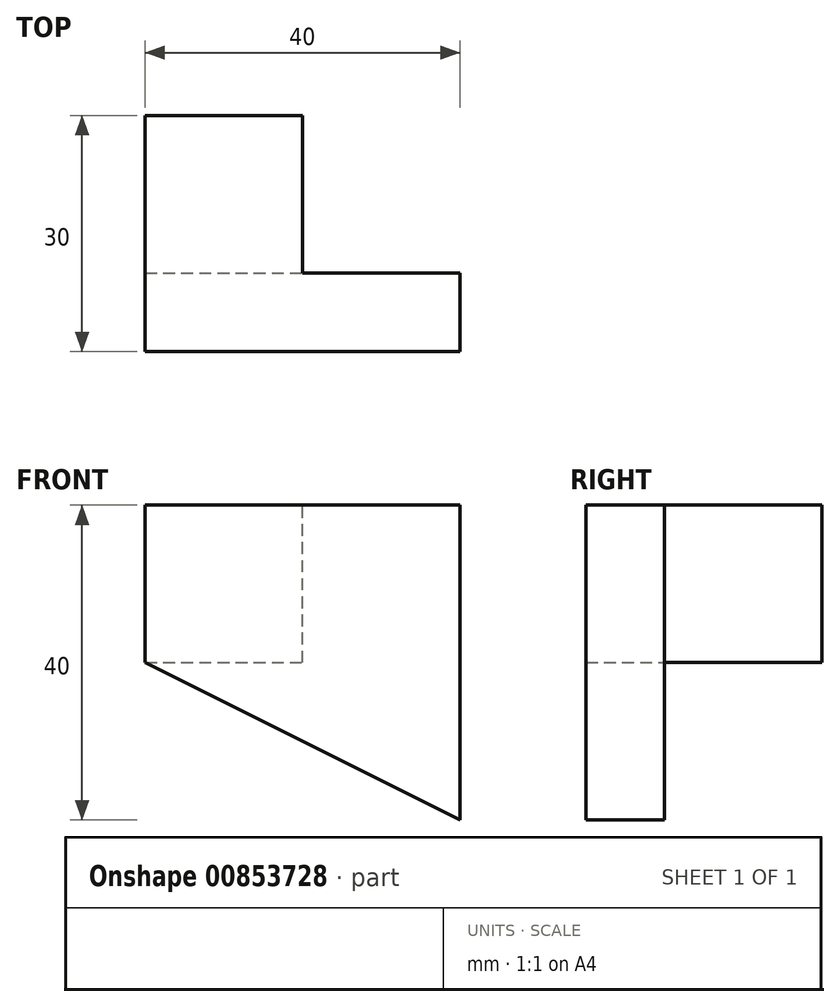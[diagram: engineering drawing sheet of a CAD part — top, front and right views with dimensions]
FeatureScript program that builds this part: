
annotation { "Feature Type Name" : "Feature", "Feature Type Description" : "" }
export const myFeature = defineFeature(function(context is Context, id is Id, definition is map)
    precondition{}
    {
        {
            var Q0;
            Q0=qCreatedBy(makeId("Front.planeOp"),FACE);
            var sketch = newSketch(context, id + "F0", { "sketchPlane" : qUnion([Q0])});
            skLineSegment(sketch, "E0.bottom", {"start": v(0, 0) * mm, "end": v(20, 0) * mm});
            skLineSegment(sketch, "E0.top", {"start": v(0, 20) * mm, "end": v(20, 20) * mm});
            skLineSegment(sketch, "E0.left", {"start": v(0, 0) * mm, "end": v(0, 20) * mm});
            skLineSegment(sketch, "E0.right", {"start": v(20, 0) * mm, "end": v(20, 20) * mm});
            skSolve(sketch);
        }
        {
            var Q0;
            Q0 = qSketchRegion(id + "F0", true);
            extrude(context, id + "F1", {"entities" : qUnion([Q0]), "depth" : 20 * mm, "offsetDistance" : 25 * mm});
        }
        {
            var Q0;
            Q0=makeQuery(id+"F1.opExtrude","CAP_FACE",FACE,{"disambiguationData":[OSD([sQuery(id+"F0.wireOp",EDGE,"E0.bottom"),sQuery(id+"F0.wireOp",EDGE,"E0.top"),sQuery(id+"F0.wireOp",EDGE,"E0.left"),sQuery(id+"F0.wireOp",EDGE,"E0.right")])],"isStart":false});
            var sketch = newSketch(context, id + "F2", { "sketchPlane" : qUnion([Q0])});
            skLineSegment(sketch, "E1.bottom", {"start": v(0, 20) * mm, "end": v(40, 20) * mm});
            skLineSegment(sketch, "E1.left", {"start": v(0, 20) * mm, "end": v(0, 0) * mm});
            skLineSegment(sketch, "E1.right", {"start": v(40, 20) * mm, "end": v(40, -20) * mm});
            skLineSegment(sketch, "E2", {"start": v(0, 0) * mm, "end": v(40, -20) * mm});
            skSolve(sketch);
        }
        {
            var Q0;
            {var subQ0=sQuery(id+"F2.wireOp",EDGE,"E1.right");Q0=makeQuery(id+"F2.imprint","IMPRINT",FACE,{"disambiguationData":[TD([[makeQuery(id+"F2.imprint","IMPRINT",EDGE,{"derivedFrom":subQ0}),-1.0]])]});}
            var Q1;
            {var subQ0=sQuery(id+"F2.wireOp",EDGE,"E1.left");Q1=makeQuery(id+"F2.imprint","IMPRINT",FACE,{"disambiguationData":[TD([[makeQuery(id+"F2.imprint","IMPRINT",EDGE,{"derivedFrom":subQ0}),-1.0]])]});}
            extrude(context, id + "F3", {"entities" : qUnion([Q0, Q1]), "operationType" : NewBodyOperationType.ADD, "depth" : 10 * mm, "offsetDistance" : 25 * mm});
        }
    });
